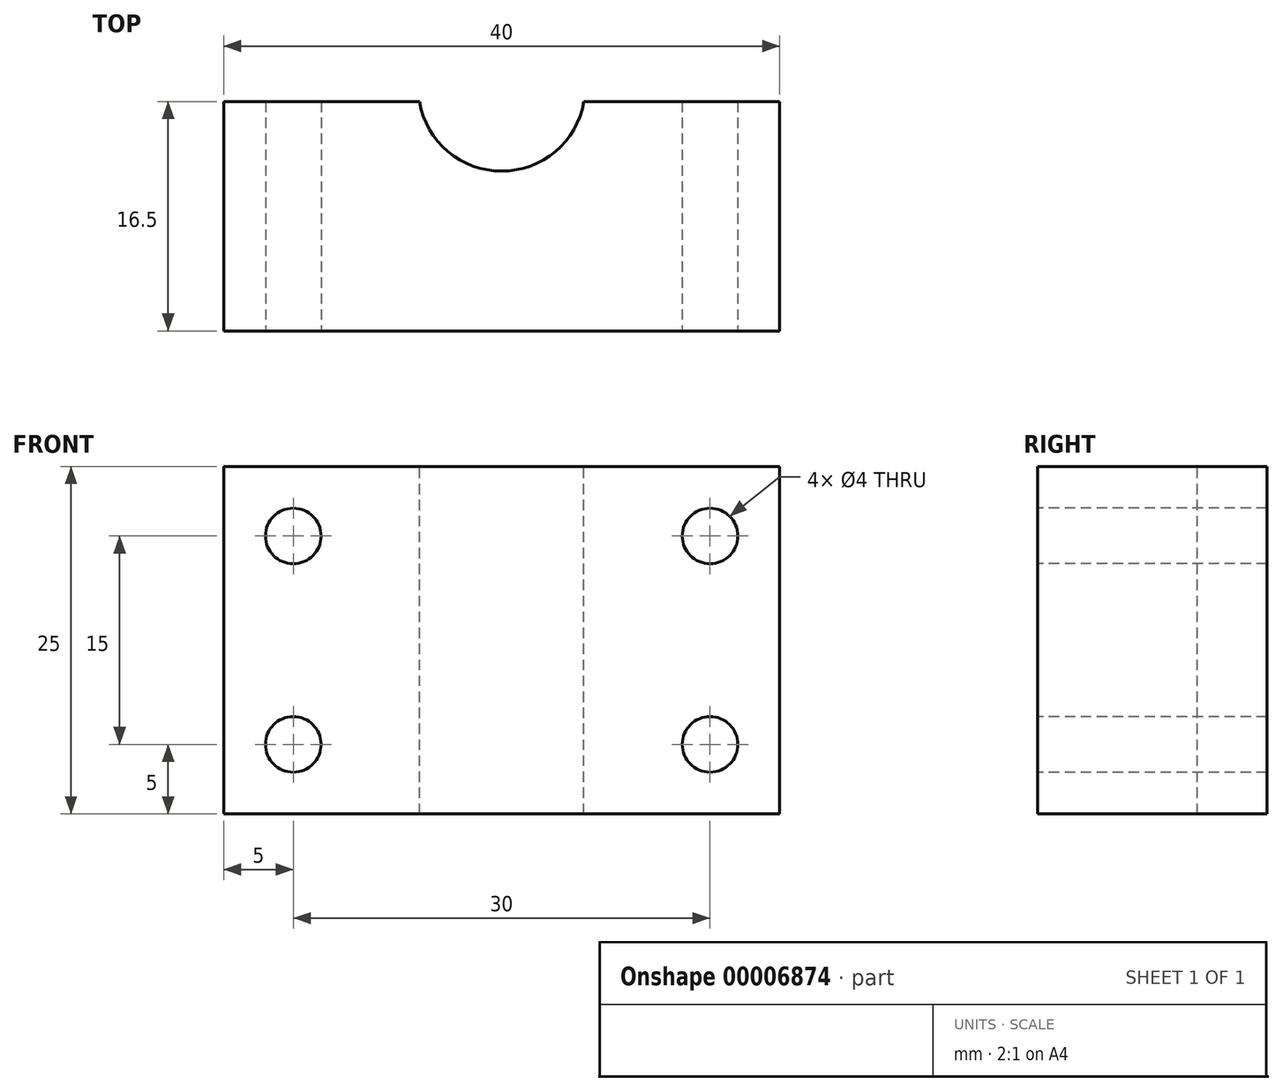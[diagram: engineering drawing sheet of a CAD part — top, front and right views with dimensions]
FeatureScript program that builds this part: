
annotation { "Feature Type Name" : "Feature", "Feature Type Description" : "" }
export const myFeature = defineFeature(function(context is Context, id is Id, definition is map)
    precondition{}
    {
        {
            var Q0;
            Q0=qCreatedBy(makeId("Top.planeOp"),FACE);
            var sketch = newSketch(context, id + "F0", { "sketchPlane" : qUnion([Q0])});
            skLineSegment(sketch, "E0.bottom", {"start": v(-20, 0) * mm, "end": v(20, 0) * mm});
            skLineSegment(sketch, "E0.top", {"start": v(-20, -17.5) * mm, "end": v(20, -17.5) * mm});
            skLineSegment(sketch, "E0.left", {"start": v(-20, 0) * mm, "end": v(-20, -17.5) * mm});
            skLineSegment(sketch, "E0.right", {"start": v(20, 0) * mm, "end": v(20, -17.5) * mm});
            skSolve(sketch);
        }
        {
            var Q0;
            Q0 = qSketchRegion(id + "F0", true);
            extrude(context, id + "F1", {"entities" : qUnion([Q0]), "depth" : 25 * mm});
        }
        {
            var Q0;
            Q0=makeQuery(id+"F1.opExtrude","SWEPT_FACE",FACE,{"disambiguationData":[OSD([sQuery(id+"F0.wireOp",EDGE,"E0.top")])]});
            var sketch = newSketch(context, id + "F2", { "sketchPlane" : qUnion([Q0])});
            skCircle(sketch, "E1", {"center": v(-15, 20) * mm, "radius": 2 * mm});
            skCircle(sketch, "E2", {"center": v(-15, 5) * mm, "radius": 2 * mm});
            skCircle(sketch, "E3", {"center": v(15, 20) * mm, "radius": 2 * mm});
            skCircle(sketch, "E4", {"center": v(15, 5) * mm, "radius": 2 * mm});
            skSolve(sketch);
        }
        {
            var Q0;
            Q0 = qSketchRegion(id + "F2", true);
            extrude(context, id + "F3", {"entities" : qUnion([Q0]), "operationType" : NewBodyOperationType.REMOVE, "oppositeDirection" : true, "depth" : 25 * mm});
        }
        {
            var Q0;
            Q0=makeQuery(id+"F1.opExtrude","CAP_FACE",FACE,{"disambiguationData":[OSD([sQuery(id+"F0.wireOp",EDGE,"E0.bottom"),sQuery(id+"F0.wireOp",EDGE,"E0.top"),sQuery(id+"F0.wireOp",EDGE,"E0.left"),sQuery(id+"F0.wireOp",EDGE,"E0.right")])],"isStart":false});
            var sketch = newSketch(context, id + "F4", { "sketchPlane" : qUnion([Q0])});
            skCircle(sketch, "E5", {"center": v(0, 0) * mm, "radius": 6 * mm});
            skSolve(sketch);
        }
        {
            var Q0;
            Q0 = qSketchRegion(id + "F4", true);
            extrude(context, id + "F5", {"entities" : qUnion([Q0]), "operationType" : NewBodyOperationType.REMOVE, "oppositeDirection" : true, "depth" : 25 * mm});
        }
        {
            var Q0;
            {var subQ0=sQuery(id+"F0.wireOp",EDGE,"E0.bottom");var subQ1=sQuery(id+"F0.wireOp",EDGE,"E0.left");Q0=makeQuery(id+"F5.boolean.opBoolean","SPLIT",FACE,{"disambiguationData":[TD([makeQuery(id+"F1.opExtrude","SWEPT_FACE",FACE,{"disambiguationData":[OSD([subQ1])]})])],"derivedFrom":makeQuery(id+"F1.opExtrude","SWEPT_FACE",FACE,{"disambiguationData":[OSD([subQ0])]})});}
            extrude(context, id + "F6", {"entities" : qUnion([Q0]), "operationType" : NewBodyOperationType.REMOVE, "oppositeDirection" : true, "depth" : (1) * mm});
        }
        {
            var Q0;
            {var subQ0=sQuery(id+"F0.wireOp",EDGE,"E0.bottom");var subQ1=sQuery(id+"F0.wireOp",EDGE,"E0.right");Q0=makeQuery(id+"F5.boolean.opBoolean","SPLIT",FACE,{"disambiguationData":[TD([makeQuery(id+"F1.opExtrude","SWEPT_FACE",FACE,{"disambiguationData":[OSD([subQ1])]})])],"derivedFrom":makeQuery(id+"F1.opExtrude","SWEPT_FACE",FACE,{"disambiguationData":[OSD([subQ0])]})});}
            extrude(context, id + "F7", {"entities" : qUnion([Q0]), "operationType" : NewBodyOperationType.REMOVE, "oppositeDirection" : true, "depth" : (1) * mm});
        }
        {
            var Q0;
            Q0=makeQuery(id+"F6.boolean.opBoolean","COPY",FACE,{"derivedFrom":makeQuery(id+"F6.opExtrude","SWEPT_FACE",FACE,{"disambiguationData":[OSD([sQuery(id+"F0.wireOp",EDGE,"E0.bottom"),sQuery(id+"F4.wireOp",EDGE,"E5")])]})});
            extrude(context, id + "F8", {"entities" : qUnion([Q0]), "operationType" : NewBodyOperationType.REMOVE, "endBound" : BoundingType.THROUGH_ALL, "oppositeDirection" : true, "depth" : 25 * mm});
        }
    });
